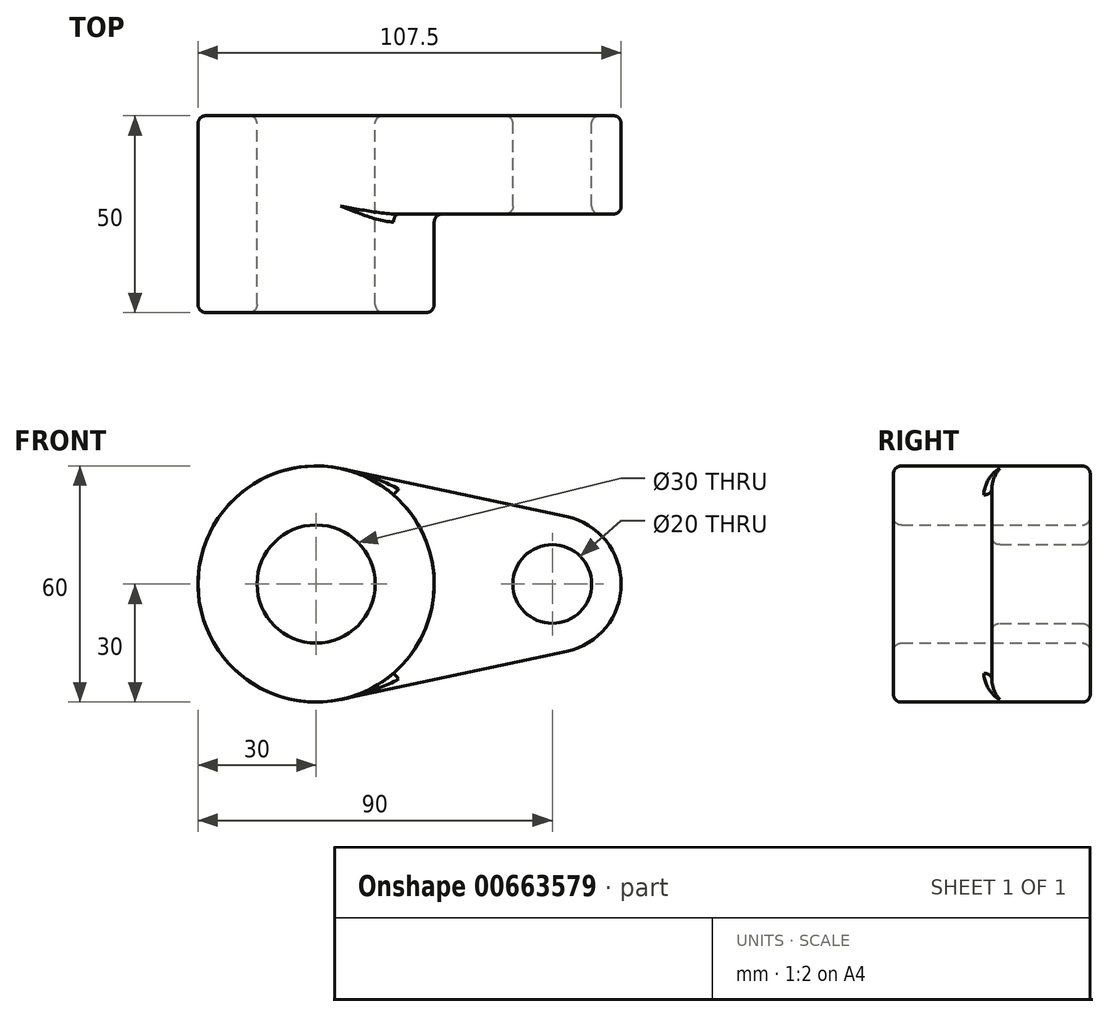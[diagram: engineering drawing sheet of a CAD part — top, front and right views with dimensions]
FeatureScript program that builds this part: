
annotation { "Feature Type Name" : "Feature", "Feature Type Description" : "" }
export const myFeature = defineFeature(function(context is Context, id is Id, definition is map)
    precondition{}
    {
        {
            var Q0;
            Q0=qCreatedBy(makeId("Front.planeOp"),FACE);
            var sketch = newSketch(context, id + "F0", { "sketchPlane" : qUnion([Q0])});
            skCircle(sketch, "E0", {"center": v(0, 0) * mm, "radius": 30 * mm});
            skCircle(sketch, "E1", {"center": v(60, 0) * mm, "radius": 17.5 * mm});
            skLineSegment(sketch, "E2", {"start": v(6.25, 29.34) * mm, "end": v(63.65, 17.12) * mm});
            skLineSegment(sketch, "E3", {"start": v(6.25, -29.34) * mm, "end": v(63.65, -17.12) * mm});
            skCircle(sketch, "E4", {"center": v(0, 0) * mm, "radius": 15 * mm});
            skCircle(sketch, "E5", {"center": v(60, 0) * mm, "radius": 10 * mm});
            skSolve(sketch);
        }
        {
            var Q0;
            Q0 = qSketchRegion(id + "F0", true);
            extrude(context, id + "F1", {"entities" : qUnion([Q0]), "depth" : 25 * mm, "offsetDistance" : 25 * mm});
        }
        {
            var Q0;
            Q0=makeQuery(id+"F0.imprint","IMPRINT",FACE,{"disambiguationData":[TD([[makeQuery(id+"F0.imprint","IMPRINT",EDGE,{"derivedFrom":sQuery(id+"F0.wireOp",EDGE,"E4")}),-1.0]])]});
            extrude(context, id + "F2", {"entities" : qUnion([Q0]), "operationType" : NewBodyOperationType.ADD, "depth" : 50 * mm, "offsetDistance" : 25 * mm});
        }
        {
            var Q0;
            Q0=makeQuery(id+"F1.opExtrude","CAP_EDGE",EDGE,{"disambiguationData":[OSD([sQuery(id+"F0.wireOp",EDGE,"E0")])],"isStart":true});
            var Q1;
            Q1=makeQuery(id+"F1.opExtrude","CAP_EDGE",EDGE,{"disambiguationData":[OSD([sQuery(id+"F0.wireOp",EDGE,"E3")])],"isStart":true});
            var Q2;
            Q2=makeQuery(id+"F1.opExtrude","CAP_EDGE",EDGE,{"disambiguationData":[OSD([sQuery(id+"F0.wireOp",EDGE,"E1")])],"isStart":true});
            var Q3;
            Q3=makeQuery(id+"F1.opExtrude","CAP_EDGE",EDGE,{"disambiguationData":[OSD([sQuery(id+"F0.wireOp",EDGE,"E2")])],"isStart":true});
            fillet(context, id + "F3", {"entities" : qUnion([Q0, Q1, Q2, Q3]), "radius" : 2 * mm, "tangentPropagation" : true, "allowEdgeOverflow" : false});
        }
        {
            var Q0;
            Q0=makeQuery(id+"F2.opExtrude","CAP_EDGE",EDGE,{"disambiguationData":[OSD([sQuery(id+"F0.wireOp",EDGE,"E0")])],"isStart":false});
            var Q1;
            Q1=makeQuery(id+"F1.opExtrude","CAP_EDGE",EDGE,{"disambiguationData":[OSD([sQuery(id+"F0.wireOp",EDGE,"E3")])],"isStart":false});
            var Q2;
            Q2=makeQuery(id+"F1.opExtrude","CAP_EDGE",EDGE,{"disambiguationData":[OSD([sQuery(id+"F0.wireOp",EDGE,"E1")])],"isStart":false});
            var Q3;
            Q3=makeQuery(id+"F1.opExtrude","CAP_FACE",FACE,{"disambiguationData":[OSD([sQuery(id+"F0.wireOp",EDGE,"E0"),sQuery(id+"F0.wireOp",EDGE,"E1"),sQuery(id+"F0.wireOp",EDGE,"E2"),sQuery(id+"F0.wireOp",EDGE,"E3"),sQuery(id+"F0.wireOp",EDGE,"E4"),sQuery(id+"F0.wireOp",EDGE,"E5")])],"isStart":false});
            fillet(context, id + "F4", {"entities" : qUnion([Q0, Q1, Q2, Q3]), "radius" : 2 * mm, "tangentPropagation" : true, "allowEdgeOverflow" : false});
        }
        {
            var Q0;
            Q0=makeQuery(id+"F2.opExtrude","CAP_EDGE",EDGE,{"disambiguationData":[OSD([sQuery(id+"F0.wireOp",EDGE,"E4")])],"isStart":false});
            var Q1;
            Q1=makeQuery(id+"F1.opExtrude","CAP_EDGE",EDGE,{"disambiguationData":[OSD([sQuery(id+"F0.wireOp",EDGE,"E4")])],"isStart":true});
            var Q2;
            Q2=makeQuery(id+"F1.opExtrude","CAP_EDGE",EDGE,{"disambiguationData":[OSD([sQuery(id+"F0.wireOp",EDGE,"E5")])],"isStart":true});
            fillet(context, id + "F5", {"entities" : qUnion([Q0, Q1, Q2]), "radius" : 2 * mm, "tangentPropagation" : true, "allowEdgeOverflow" : false});
        }
    });
